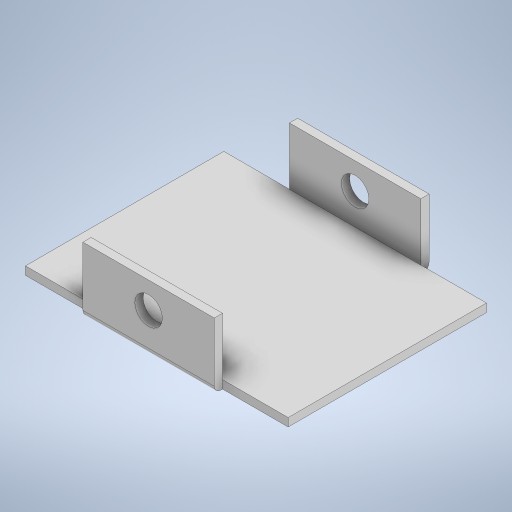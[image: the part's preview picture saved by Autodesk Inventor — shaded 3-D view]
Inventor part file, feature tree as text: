
AUTODESK INVENTOR PART (.ipt)
format: ipt  version: 2024 (Build 280153000, 153)  size: 262,144 bytes
history: native  units: in
note: dims shown in document units (in); Inventor stores cm internally (conversion verified against a paired STEP export)
features: extrude x4, sketch x4, fillet x1
ambient origin geometry x8: Origin, YZ Plane, XZ Plane, XY Plane, X Axis, Y Axis, Z Axis, Center Point
bodies: Solid1 (feature_tree)
feature tree (9):
  extrude  "Extrusion1"  Depth=1.51in
  extrude  "Extrusion2"  Depth=0.5in
  extrude  "Extrusion3"  Depth=0.5in
  extrude  "Extrusion4"  Depth=0.5in
  fillet  "Fillet1"  Radius=1.0in
  sketch  "Sketch1"  dims[d0=2.0in d1=1.51in]
  sketch  "Sketch2"  dims[d2=0.0625in d3=0.0in d4=0.5in]
  sketch  "Sketch3"  dims[d5=1.0in d6=0.5in]
  sketch  "Sketch4"  dims[d7=0.0625in d8=0.0in d9=0.5in d10=1.0in d11=0.5in d12=1.0in d13=0.0625in d14=0.0in d15=0.5in d16=0.2in d17=0.21in d18=2.0in d19=0.0in d20=0.05in]
